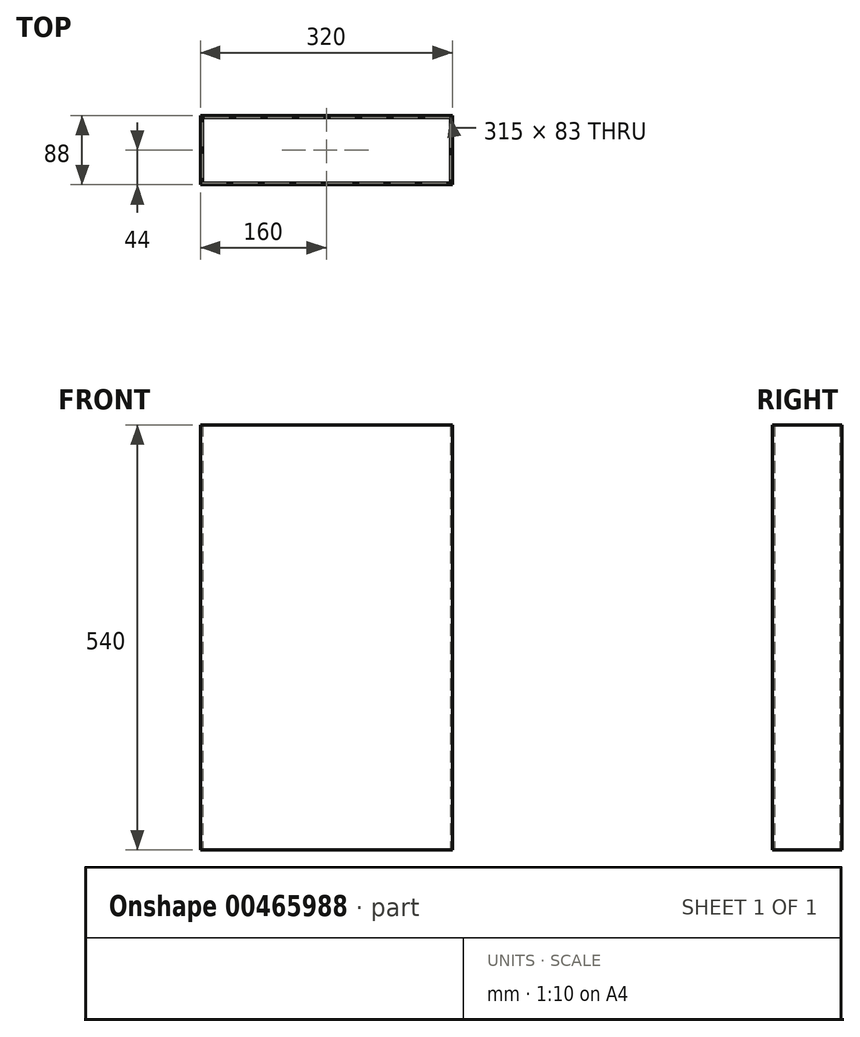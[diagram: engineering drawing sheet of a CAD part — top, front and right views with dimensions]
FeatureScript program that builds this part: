
annotation { "Feature Type Name" : "Feature", "Feature Type Description" : "" }
export const myFeature = defineFeature(function(context is Context, id is Id, definition is map)
    precondition{}
    {
        {
            var Q0;
            Q0=qCreatedBy(makeId("Front.planeOp"),FACE);
            var sketch = newSketch(context, id + "F0", { "sketchPlane" : qUnion([Q0])});
            skLineSegment(sketch, "E0.bottom", {"start": v(-160, 540) * mm, "end": v(160, 540) * mm});
            skLineSegment(sketch, "E0.top", {"start": v(-160, 0) * mm, "end": v(160, 0) * mm});
            skLineSegment(sketch, "E0.left", {"start": v(-160, 540) * mm, "end": v(-160, 0) * mm});
            skLineSegment(sketch, "E0.right", {"start": v(160, 540) * mm, "end": v(160, 0) * mm});
            skSolve(sketch);
        }
        {
            var Q0;
            Q0 = qSketchRegion(id + "F0", true);
            extrude(context, id + "F1", {"entities" : qUnion([Q0]), "depth" : 88 * mm});
        }
        {
            var Q0;
            Q0=makeQuery(id+"F1.opExtrude","SWEPT_FACE",FACE,{"disambiguationData":[OSD([sQuery(id+"F0.wireOp",EDGE,"E0.bottom")])]});
            var Q1;
            Q1=makeQuery(id+"F1.opExtrude","SWEPT_FACE",FACE,{"disambiguationData":[OSD([sQuery(id+"F0.wireOp",EDGE,"E0.top")])]});
            shell(context, id + "F2", {"entities" : qUnion([Q0, Q1]), "thickness" : 2.5 * mm});
        }
    });
